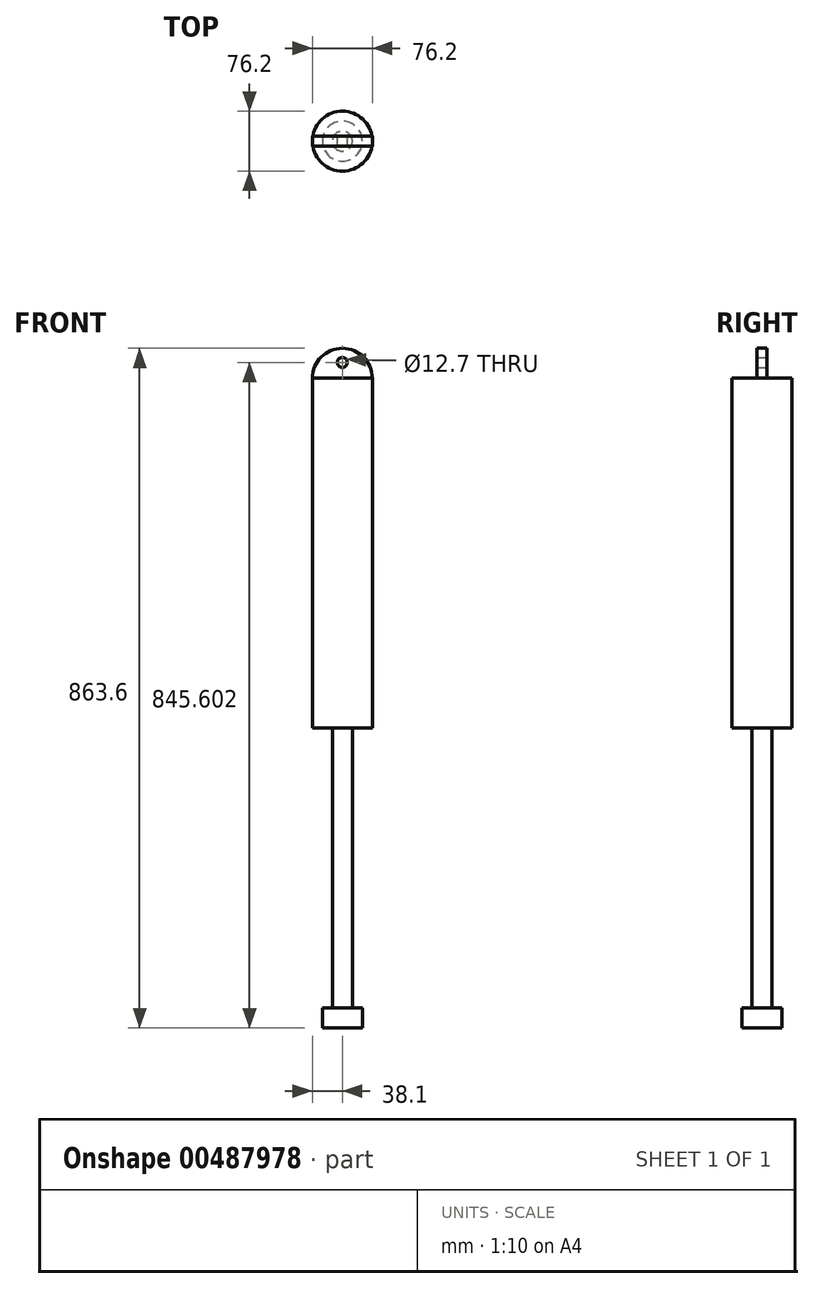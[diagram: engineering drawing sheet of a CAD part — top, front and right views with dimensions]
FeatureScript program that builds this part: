
annotation { "Feature Type Name" : "Feature", "Feature Type Description" : "" }
export const myFeature = defineFeature(function(context is Context, id is Id, definition is map)
    precondition{}
    {
        {
            var Q0;
            Q0=qCreatedBy(makeId("Front.planeOp"),FACE);
            var sketch = newSketch(context, id + "F0", { "sketchPlane" : qUnion([Q0])});
            skLineSegment(sketch, "E0.bottom", {"start": v(0, 0) * mm, "end": v(12.7, 0) * mm});
            skLineSegment(sketch, "E0.top", {"start": v(0, -355.6) * mm, "end": v(12.7, -355.6) * mm});
            skLineSegment(sketch, "E0.left", {"start": v(0, 0) * mm, "end": v(0, -355.6) * mm});
            skLineSegment(sketch, "E0.right", {"start": v(12.7, 0) * mm, "end": v(12.7, -355.6) * mm});
            skLineSegment(sketch, "E1.bottom", {"start": v(0, 0) * mm, "end": v(38.1, 0) * mm});
            skLineSegment(sketch, "E1.top", {"start": v(0, 444.5) * mm, "end": v(38.1, 444.5) * mm});
            skLineSegment(sketch, "E1.left", {"start": v(0, 0) * mm, "end": v(0, 444.5) * mm});
            skLineSegment(sketch, "E1.right", {"start": v(38.1, 0) * mm, "end": v(38.1, 444.5) * mm});
            skLineSegment(sketch, "E2.bottom", {"start": v(0, -355.6) * mm, "end": v(25.4, -355.6) * mm});
            skLineSegment(sketch, "E2.top", {"start": v(0, -381) * mm, "end": v(25.4, -381) * mm});
            skLineSegment(sketch, "E2.left", {"start": v(0, -355.6) * mm, "end": v(0, -381) * mm});
            skLineSegment(sketch, "E2.right", {"start": v(25.4, -355.6) * mm, "end": v(25.4, -381) * mm});
            skArc(sketch, "E3", {"start": v(38.1, 444.5) * mm, "mid": v(0, 482.6) * mm, "end": v(-38.1, 444.5) * mm});
            skLineSegment(sketch, "E4", {"start": v(-38.1, 444.5) * mm, "end": v(0, 444.5) * mm});
            skCircle(sketch, "E5", {"center": v(0, 464.6) * mm, "radius": 6.35 * mm});
            skLineSegment(sketch, "E6", {"start": v(0, -381) * mm, "end": v(12.7, -381) * mm});
            skLineSegment(sketch, "E7", {"start": v(12.7, -381) * mm, "end": v(12.7, -469.9) * mm});
            skArc(sketch, "E8", {"start": v(-12.7, -469.81) * mm, "mid": v(0, -482.56) * mm, "end": v(12.7, -469.81) * mm});
            skLineSegment(sketch, "E9", {"start": v(-12.7, -469.9) * mm, "end": v(-12.7, -381) * mm});
            skLineSegment(sketch, "E10", {"start": v(-12.7, -381) * mm, "end": v(0, -381) * mm});
            skCircle(sketch, "E11", {"center": v(0, -469.86) * mm, "radius": 6.35 * mm});
            skSolve(sketch);
        }
        {
            var Q0;
            Q0=makeQuery(id+"F0.imprint","IMPRINT",FACE,{"disambiguationData":[TD([[makeQuery(id+"F0.imprint","IMPRINT",EDGE,{"derivedFrom":sQuery(id+"F0.wireOp",EDGE,"E1.top")}),1.0]])]});
            var Q1;
            Q1=makeQuery(id+"F0.imprint","IMPRINT",FACE,{"disambiguationData":[TD([[makeQuery(id+"F0.imprint","IMPRINT",EDGE,{"derivedFrom":sQuery(id+"F0.wireOp",EDGE,"E6")}),-1.0]])]});
            extrude(context, id + "F1", {"entities" : qUnion([Q0, Q1]), "endBound" : BoundingType.SYMMETRIC, "depth" : 12.7 * mm});
        }
        {
            var Q0;
            Q0=makeQuery(id+"F0.imprint","IMPRINT",FACE,{"disambiguationData":[TD([[makeQuery(id+"F0.imprint","IMPRINT",EDGE,{"derivedFrom":sQuery(id+"F0.wireOp",EDGE,"E1.top")}),-1.0]])]});
            var Q1;
            {var subQ0=sQuery(id+"F0.wireOp",EDGE,"E0.left");Q1=makeQuery(id+"F0.imprint","IMPRINT",FACE,{"disambiguationData":[TD([[makeQuery(id+"F0.imprint","IMPRINT",EDGE,{"derivedFrom":subQ0}),1.0]])]});}
            var Q2;
            Q2=makeQuery(id+"F0.imprint","IMPRINT",FACE,{"disambiguationData":[TD([[makeQuery(id+"F0.imprint","IMPRINT",EDGE,{"derivedFrom":sQuery(id+"F0.wireOp",EDGE,"E2.top")}),1.0]])]});
            var Q3;
            Q3=sQuery(id+"F0.wireOp",EDGE,"E2.left");
            revolve(context, id + "F2", {"entities" : qUnion([Q0, Q1, Q2]), "axis" : qUnion([Q3]), "revolveType" : RevolveType.FULL});
        }
    });
